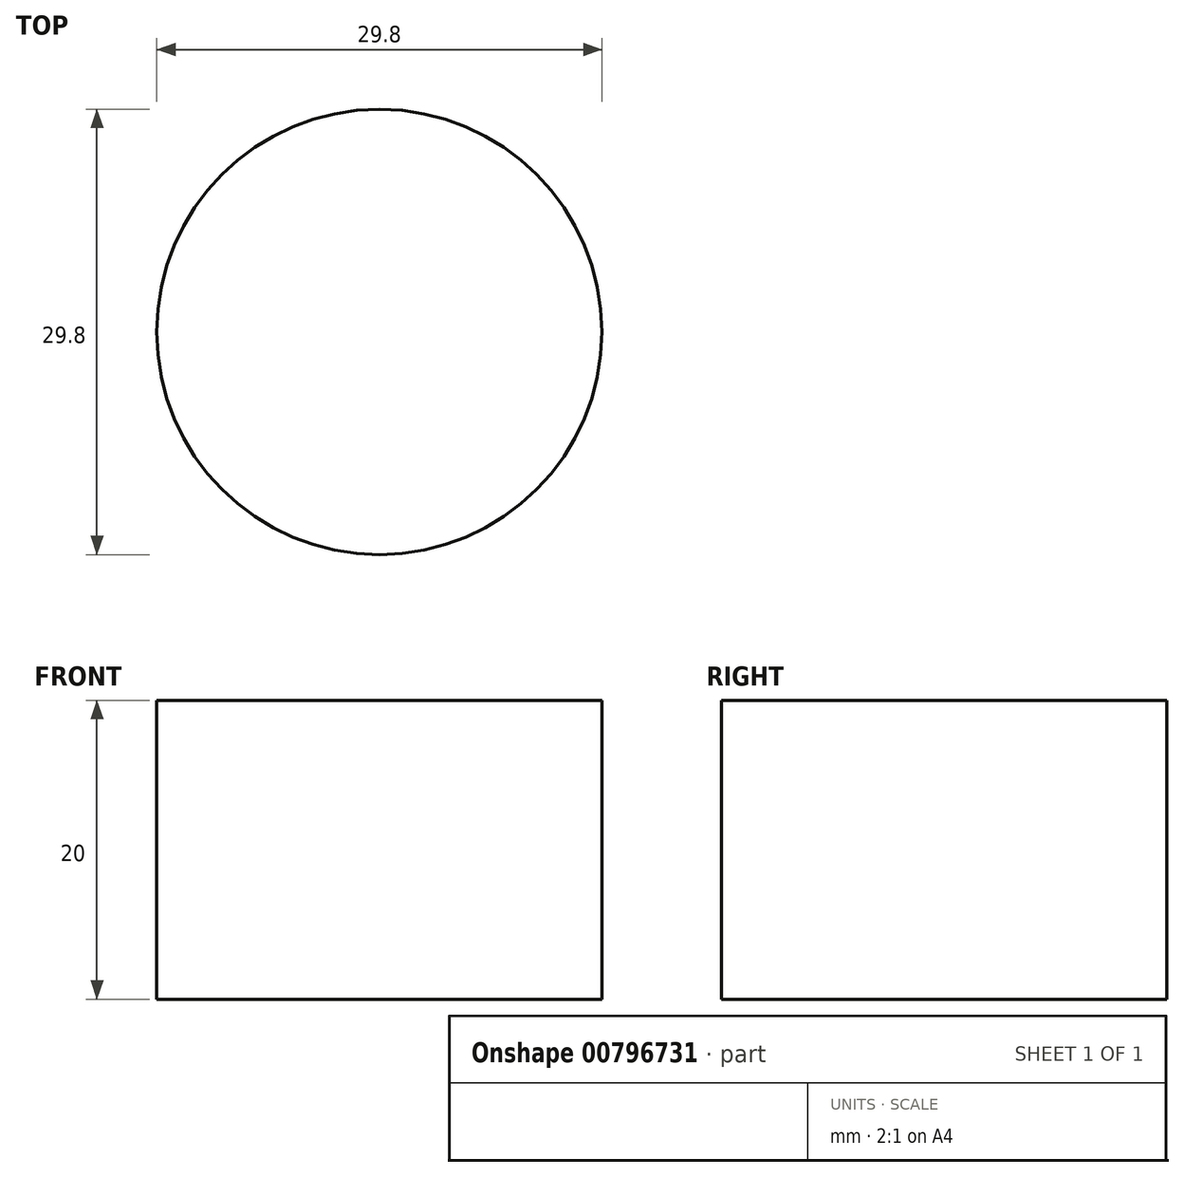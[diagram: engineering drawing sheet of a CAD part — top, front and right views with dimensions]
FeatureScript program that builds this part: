
annotation { "Feature Type Name" : "Feature", "Feature Type Description" : "" }
export const myFeature = defineFeature(function(context is Context, id is Id, definition is map)
    precondition{}
    {
        {
            var Q0;
            Q0=qCreatedBy(makeId("Top.planeOp"),FACE);
            var sketch = newSketch(context, id + "F0", { "sketchPlane" : qUnion([Q0])});
            skLineSegment(sketch, "E0", {"start": v(0, 75.03) * mm, "end": v(0, -74.61) * mm, "construction": true});
            skSolve(sketch);
        }
        {
            var Q0;
            Q0=qCreatedBy(makeId("Top.planeOp"),FACE);
            var sketch = newSketch(context, id + "F1", { "sketchPlane" : qUnion([Q0])});
            skCircle(sketch, "E1", {"center": v(-15.05, -25.95) * mm, "radius": 15 * mm});
            skCircle(sketch, "E2", {"center": v(14.95, -26.06) * mm, "radius": 15 * mm});
            skCircle(sketch, "E3", {"center": v(-0.1, 0.05) * mm, "radius": 15 * mm});
            skCircle(sketch, "E4.MirrorC", {"center": v(15.05, -25.95) * mm, "radius": 15 * mm});
            skSolve(sketch);
        }
        {
            var Q0;
            Q0=qCreatedBy(makeId("Top.planeOp"),FACE);
            var sketch = newSketch(context, id + "F2", { "sketchPlane" : qUnion([Q0])});
            skCircle(sketch, "E5", {"center": v(29.9, 0) * mm, "radius": 15 * mm});
            skCircle(sketch, "E6.MirrorC", {"center": v(-30.1, 0) * mm, "radius": 15 * mm});
            skSolve(sketch);
        }
        {
            var Q0;
            Q0=qCreatedBy(makeId("Top.planeOp"),FACE);
            var sketch = newSketch(context, id + "F3", { "sketchPlane" : qUnion([Q0])});
            skCircle(sketch, "E7", {"center": v(-30.1, 0) * mm, "radius": 14.9 * mm});
            skSolve(sketch);
        }
        {
            var Q0;
            Q0=sQuery(id+"F2.wireOp",EDGE,"E6.MirrorC");
            extrude(context, id + "F4", {"bodyType" : ToolBodyType.SURFACE, "surfaceEntities" : qUnion([Q0]), "depth" : 20 * mm, "offsetDistance" : 25 * mm});
        }
        {
            var Q0;
            Q0=makeQuery(id+"F3.imprint","IMPRINT",FACE,{"disambiguationData":[TD([[makeQuery(id+"F3.imprint","IMPRINT",EDGE,{"derivedFrom":sQuery(id+"F3.wireOp",EDGE,"E7")}),1.0]])]});
            extrude(context, id + "F5", {"entities" : qUnion([Q0]), "depth" : 20 * mm, "offsetDistance" : 25 * mm});
        }
    });
